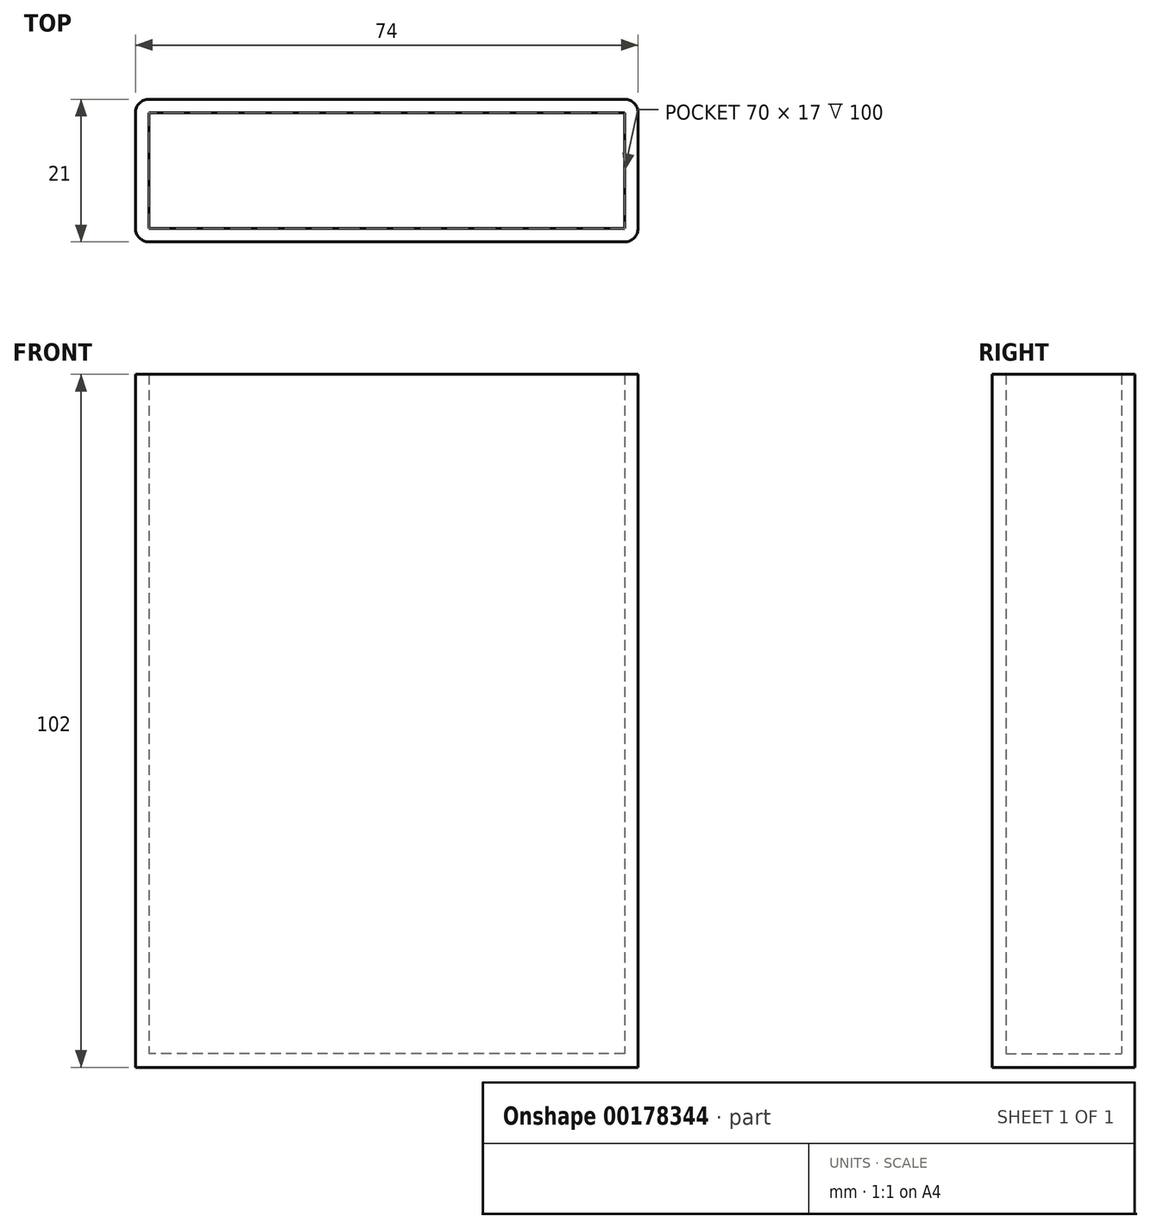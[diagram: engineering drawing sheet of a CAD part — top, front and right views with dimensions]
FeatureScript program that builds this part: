
annotation { "Feature Type Name" : "Feature", "Feature Type Description" : "" }
export const myFeature = defineFeature(function(context is Context, id is Id, definition is map)
    precondition{}
    {
        {
            var Q0;
            Q0=qCreatedBy(makeId("Top.planeOp"),FACE);
            var sketch = newSketch(context, id + "F0", { "sketchPlane" : qUnion([Q0])});
            skLineSegment(sketch, "E0.bottom", {"start": v(35, -8.5) * mm, "end": v(-35, -8.5) * mm});
            skLineSegment(sketch, "E0.top", {"start": v(35, 8.5) * mm, "end": v(-35, 8.5) * mm});
            skLineSegment(sketch, "E0.left", {"start": v(35, -8.5) * mm, "end": v(35, 8.5) * mm});
            skLineSegment(sketch, "E0.right", {"start": v(-35, -8.5) * mm, "end": v(-35, 8.5) * mm});
            skPoint(sketch, "E0.middle", {"position": v(0, 0) * mm});
            skLineSegment(sketch, "E1.0", {"start": v(35, 10.5) * mm, "end": v(-35, 10.5) * mm});
            skLineSegment(sketch, "E1.1", {"start": v(37, -8.5) * mm, "end": v(37, 8.5) * mm});
            skLineSegment(sketch, "E1.2", {"start": v(35, -10.5) * mm, "end": v(-35, -10.5) * mm});
            skLineSegment(sketch, "E1.3", {"start": v(-37, -8.5) * mm, "end": v(-37, 8.5) * mm});
            skPoint(sketch, "E2.visualSharp", {"position": v(-37, 10.5) * mm});
            skArc(sketch, "E2.filletArc", {"start": v(-35, 10.5) * mm, "mid": v(-36.41, 9.91) * mm, "end": v(-37, 8.5) * mm});
            skPoint(sketch, "E3.visualSharp", {"position": v(-37, -10.5) * mm});
            skArc(sketch, "E3.filletArc", {"start": v(-37, -8.5) * mm, "mid": v(-36.41, -9.91) * mm, "end": v(-35, -10.5) * mm});
            skPoint(sketch, "E4.visualSharp", {"position": v(37, -10.5) * mm});
            skArc(sketch, "E4.filletArc", {"start": v(35, -10.5) * mm, "mid": v(36.41, -9.91) * mm, "end": v(37, -8.5) * mm});
            skPoint(sketch, "E5.visualSharp", {"position": v(37, 10.5) * mm});
            skArc(sketch, "E5.filletArc", {"start": v(37, 8.5) * mm, "mid": v(36.41, 9.91) * mm, "end": v(35, 10.5) * mm});
            skSolve(sketch);
        }
        {
            var Q0;
            Q0=makeQuery(id+"F0.imprint","IMPRINT",FACE,{"disambiguationData":[TD([[makeQuery(id+"F0.imprint","IMPRINT",EDGE,{"derivedFrom":sQuery(id+"F0.wireOp",EDGE,"E0.bottom")}),-1.0]])]});
            extrude(context, id + "F1", {"entities" : qUnion([Q0]), "oppositeDirection" : true, "depth" : 2 * mm});
        }
        {
            var Q0;
            Q0 = qSketchRegion(id + "F0", true);
            extrude(context, id + "F2", {"entities" : qUnion([Q0]), "operationType" : NewBodyOperationType.ADD, "depth" : 100 * mm, "hasSecondDirection" : true, "secondDirectionOppositeDirection" : true, "secondDirectionDepth" : 2 * mm});
        }
    });
